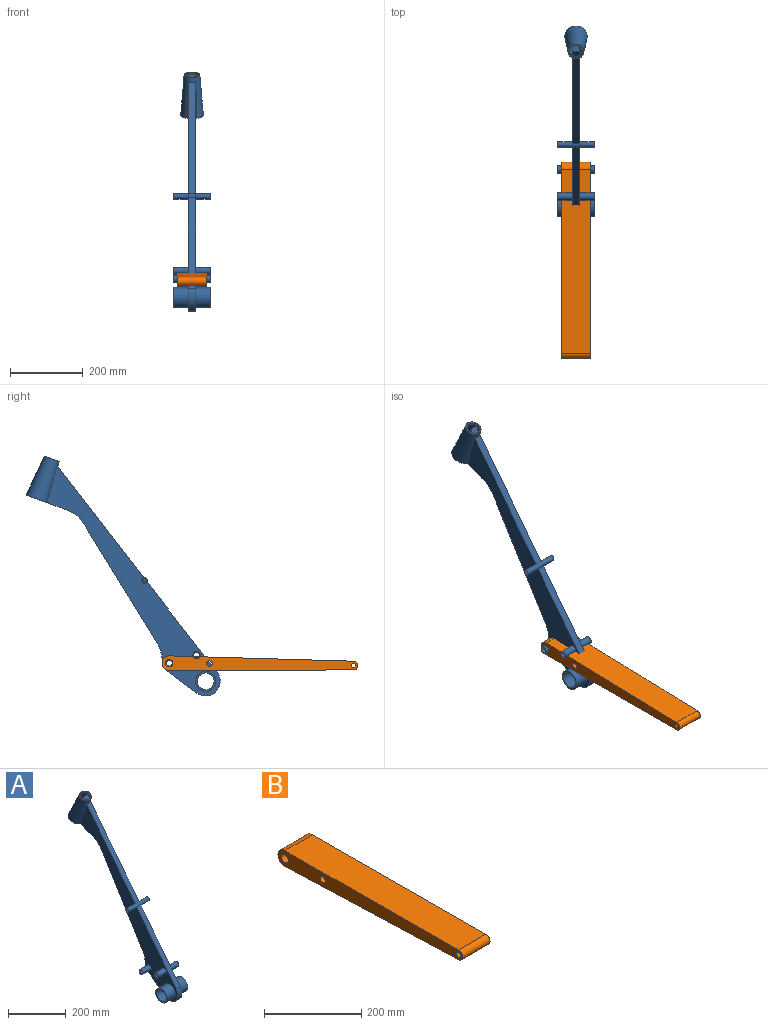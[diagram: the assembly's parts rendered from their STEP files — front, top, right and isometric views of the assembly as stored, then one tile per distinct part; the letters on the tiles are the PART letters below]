
ASSEMBLY  parts=2 mates=1
PART A: 44 faces, bbox 100x533.1x658.6 mm
  f0: cone r=21.71mm half-angle=4.5deg, axis (0,0.35,-0.94), area 209.3mm2, adj f1,f2,f12
  f1: cone r=21.71mm half-angle=4.5deg, axis (0,0.35,-0.94), area 17144.8mm2, adj f0,f2,f7,f13,f27
  f2: plane 113.12x62mm, normal (0,0.35,-0.94), area 2588.6mm2, adj f0,f1,f3,f8,f9,f10,f12,f13
  f3: cylinder r=26mm len=52mm, axis (0,-0.35,0.94), area 714.2mm2, adj f2,f4,f5,f9,f10
  f4: cone r=17.5mm half-angle=4.5deg, axis (0,0.35,-0.94), area 12312.6mm2, adj f3,f5,f6,f9,f11
  f5: cone r=17.5mm half-angle=4.5deg, axis (0,0.35,-0.94), area 274.1mm2, adj f3,f4,f10
  f6: cylinder r=17.5mm len=35mm, axis (0,-0.35,0.94), area 549.8mm2, adj f4,f7
  f7: plane 43.42x40.67mm, normal (0,-0.35,0.94), area 518.3mm2, adj f1,f6
  f8: plane 109.89x41.09mm, normal (0,0.94,0.35), area 2346.4mm2, adj f2,f9,f10,f11
  f9: plane 118.3x51.72mm, normal (-1,0,0), area 2195.5mm2, adj f2,f3,f4,f8,f11
  f10: plane 118.3x51.72mm, normal (1,0,0), area 2195.5mm2, adj f2,f3,f5,f8,f11
  f11: plane 20x16.71mm, normal (0,-0.79,0.61), area 398.6mm2, adj f4,f8,f9,f10
  f12: plane 632.06x476.6mm, normal (1,0,0), area 46549.1mm2, adj f0,f2,f16,f19,f20,f21,f22,f23
  f13: plane 632.06x476.6mm, normal (-1,0,0), area 46549.1mm2, adj f1,f2,f14,f19,f20,f21,f22,f23
  f14: cylinder r=28mm len=56mm, axis (-1,0,0), area 7037.2mm2, adj f13,f18
  f15: cylinder r=23mm len=100mm, axis (-1,0,0), area 14451.3mm2, adj f17,f18
  f16: cylinder r=28mm len=56mm, axis (-1,0,0), area 7037.2mm2, adj f12,f17
  f17: plane 56x56mm, normal (1,0,0), area 801.1mm2, adj f15,f16
  f18: plane 56x56mm, normal (-1,0,0), area 801.1mm2, adj f14,f15
  f19: cylinder r=7.5mm len=100mm, axis (-1,0,0), area 4121.4mm2, adj f12,f13,f20,f27,f29,f32
  f20: plane 248.87x192.91mm, normal (0,-0.79,0.61), area 6297.6mm2, adj f12,f13,f19,f21
  f21: cylinder r=40mm len=64.51mm, axis (-1,0,0), area 2299mm2, adj f12,f13,f20,f22
  f22: plane 88x66mm, normal (0,0.6,-0.8), area 2200mm2, adj f12,f13,f21,f23
  f23: cylinder r=20mm len=20mm, axis (-1,0,0), area 398.9mm2, adj f12,f13,f22,f24
  f24: cylinder r=87.35mm len=51.79mm, axis (-1,0,0), area 1083.7mm2, adj f12,f13,f23,f25
  f25: plane 328.99x201.86mm, normal (0,0.85,-0.52), area 7719.6mm2, adj f12,f13,f24,f26
  f26: cylinder r=90.63mm len=45.51mm, axis (-1,0,0), area 1201.1mm2, adj f2,f12,f13,f25
  f27: plane 307.76x238.56mm, normal (0,-0.79,0.61), area 7749.2mm2, adj f1,f12,f13,f19
  f28: cylinder r=5.5mm len=40mm, axis (-1,0,0), area 1382.3mm2, adj f29,f30
  f29: plane 15x15mm, normal (-1,0,0), area 81.7mm2, adj f19,f28
  f30: plane 11x11mm, normal (-1,0,0), area 95mm2, adj f28
  f31: cylinder r=5.5mm len=40mm, axis (-1,0,0), area 1382.3mm2, adj f32,f33
  f32: plane 15x15mm, normal (1,0,0), area 81.7mm2, adj f19,f31
  f33: plane 11x11mm, normal (1,0,0), area 95mm2, adj f31
  f34: cylinder r=10mm len=40mm, axis (-1,0,0), area 2513.3mm2, adj f12,f37
  f35: cylinder r=8mm len=100mm, axis (-1,0,0), area 5026.5mm2, adj f37,f38
  f36: cylinder r=10mm len=40mm, axis (-1,0,0), area 2513.3mm2, adj f13,f38
  f37: plane 20x20mm, normal (1,0,0), area 113.1mm2, adj f34,f35
  f38: plane 20x20mm, normal (-1,0,0), area 113.1mm2, adj f35,f36
  f39: cylinder r=10mm len=40mm, axis (-1,0,0), area 2513.3mm2, adj f12,f42
  f40: cylinder r=8mm len=100mm, axis (-1,0,0), area 5026.5mm2, adj f42,f43
  f41: cylinder r=10mm len=40mm, axis (-1,0,0), area 2513.3mm2, adj f13,f43
  f42: plane 20x20mm, normal (1,0,0), area 113.1mm2, adj f39,f40
  f43: plane 20x20mm, normal (-1,0,0), area 113.1mm2, adj f40,f41
PART B: 9 faces, bbox 80x537.6x42 mm
  f0: plane 505.62x80mm, normal (0,0,1), area 40449.7mm2, adj f1,f6,f7,f8
  f1: cylinder r=12mm len=80mm, axis (-1,0,0), area 2985.6mm2, adj f0,f2,f7,f8
  f2: plane 505.3x80mm, normal (0,-0.04,-1), area 40449.7mm2, adj f1,f6,f7,f8
  f3: cylinder r=6mm len=80mm, axis (-1,0,0), area 3015.9mm2, adj f7,f8
  f4: cylinder r=10mm len=80mm, axis (-1,0,0), area 5026.5mm2, adj f7,f8
  f5: cylinder r=7.5mm len=80mm, axis (-1,0,0), area 3769.9mm2, adj f7,f8
  f6: cylinder r=20mm len=80mm, axis (-1,0,0), area 5077.2mm2, adj f0,f2,f7,f8
  f7: plane 537.59x42mm, normal (1,0,0), area 16434.5mm2, adj f0,f1,f2,f3,f4,f5,f6
  f8: plane 537.59x42mm, normal (-1,0,0), area 16434.5mm2, adj f0,f1,f2,f3,f4,f5,f6
PLACE A t=(-15.6,684.43,59.29)mm fixed
PLACE B rot(axis=(1,0,0),1.9deg) t=(-15.6,683.79,78.39)mm
MATE revolute B.f4 <-> A.f23  axis (-1,0,0) through (-15.6,100.97,49.29)mm
